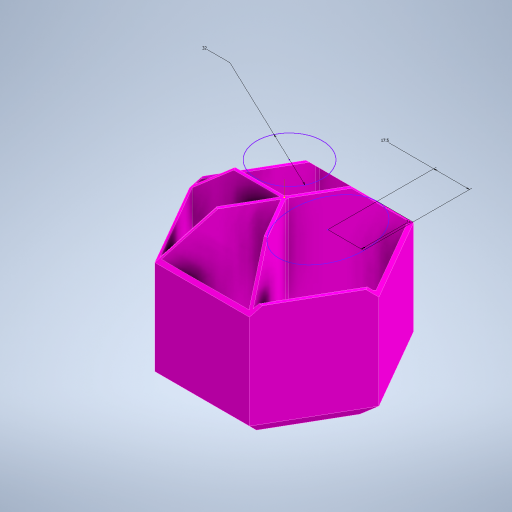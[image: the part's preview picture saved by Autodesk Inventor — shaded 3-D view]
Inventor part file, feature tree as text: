
AUTODESK INVENTOR PART (.ipt)
format: ipt  version: 2023 (Build 270158030, 158C)  size: 412,672 bytes
history: native  units: mm
features: projected_geometry x8, sketch x5, extrude x4, chamfer x4, other x1, pattern_circular x1
ambient origin geometry x8: Origin, YZ Plane, XZ Plane, XY Plane, X Axis, Y Axis, Z Axis, Center Point
bodies: Body1 (feature_tree)
feature tree (23):
  other  "pen-pot-body"
  extrude  "Extrusion1"  TaperAngle=60.0deg  [1 undecoded]
  extrude  "Extrusion2"  Depth=1.5mm
  extrude  "Extrusion3"  Depth=80.0mm
  pattern_circular  "Circular Pattern1"  Count=6 Angle=360.0deg
  chamfer  "Chamfer2"  Distance=70.0mm
  chamfer  "Chamfer1"  Distance=3.0mm
  chamfer  "Chamfer3"  Distance=8.0mm Angle=45.0deg
  chamfer  "Chamfer4"  Distance=7.0mm Angle=45.0deg
  extrude  "Extrusion4"  Depth=70.0mm TaperAngle=0.0deg
  sketch  "Sketch6"  dims[d31=19.0mm d32=2.0mm d33=45.0deg d34=15.0mm d35=0.0mm d36=32.0mm d37=24.0mm d38=17.5mm d41=20.0mm d42=240.0deg]
  sketch  "Sketch1"  dims[d5=60.0deg d6=60.0deg]
  sketch  "Sketch2"  dims[d7=0.75mm d8=1.5mm]
  projected_geometry  "Projected Loop1"
  sketch  "Sketch4"  dims[d9=1.3mm d10=80.0mm d11=60.0mm d13=360.0deg d16=70.0mm d17=0.0mm d18=3.0mm d19=0.0mm d20=8.0mm d21=2.0mm d22=45.0deg d23=7.0mm d24=2.0mm d25=45.0deg]
  projected_geometry  "Projected Loop3"
  sketch  "Sketch5"  dims[d26=19.0mm d27=2.0mm d28=45.0deg d29=70.0mm d30=0.0mm]
  projected_geometry  "Projected Loop4"
  projected_geometry  "Projected Loop5"
  projected_geometry  "Projected Loop6"
  projected_geometry  "Projected Loop7"
  projected_geometry  "Projected Loop8"
  projected_geometry  "Projected Loop9"
note: 1 required parameter value undecoded (feature->parameter linkage not recoverable at this tier; creation-order binding heuristic only, values carry confidence <= 0.55)
